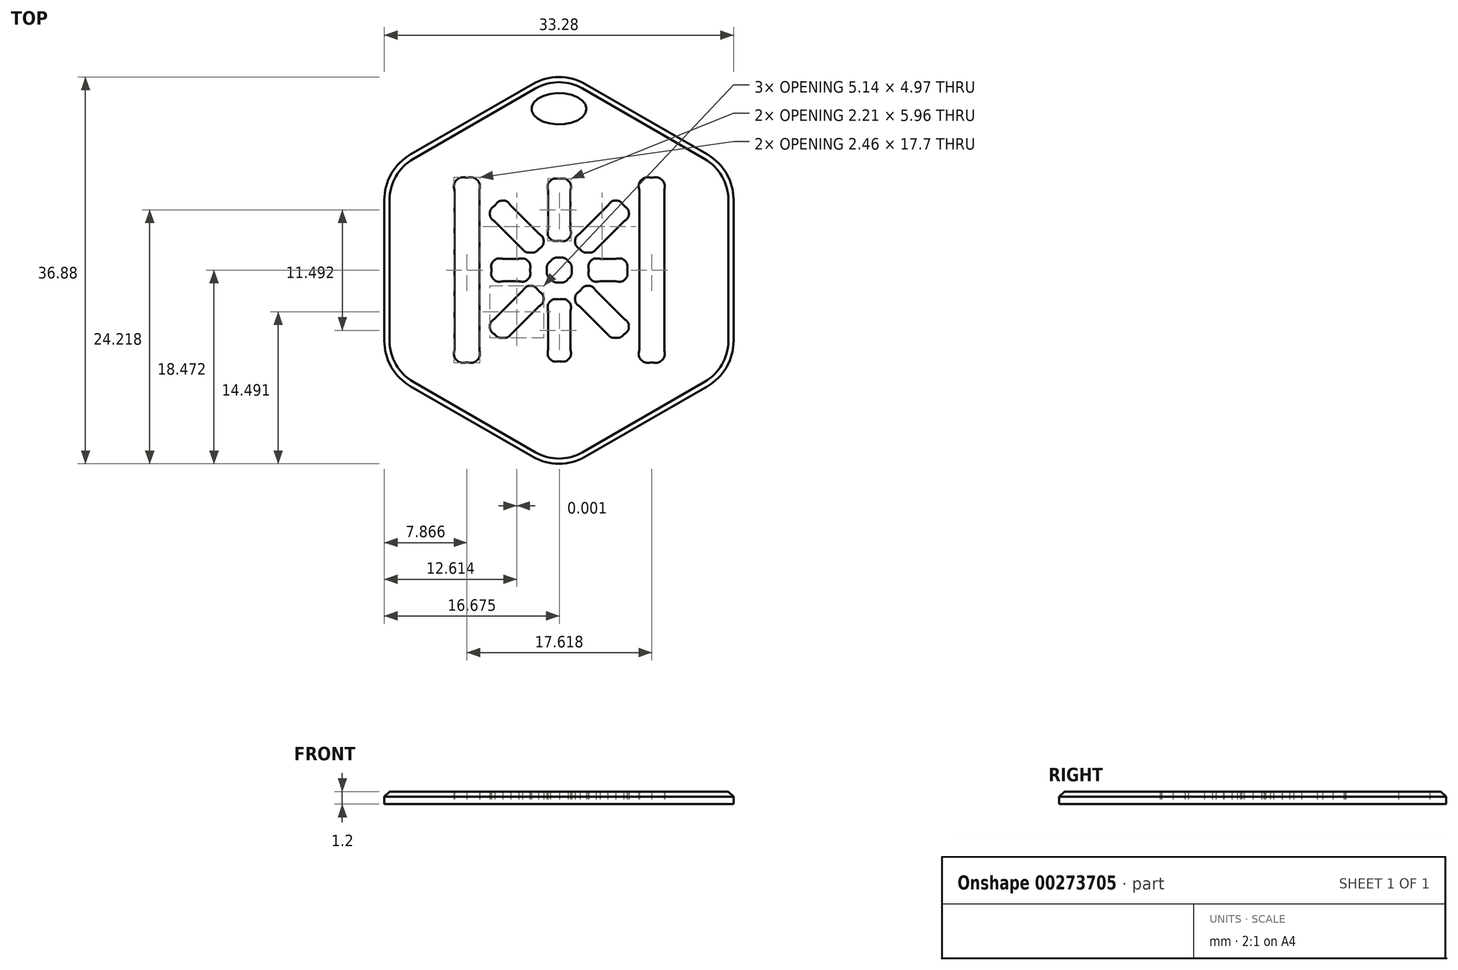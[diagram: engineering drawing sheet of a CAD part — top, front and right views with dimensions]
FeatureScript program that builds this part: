
annotation { "Feature Type Name" : "Feature", "Feature Type Description" : "" }
export const myFeature = defineFeature(function(context is Context, id is Id, definition is map)
    precondition{}
    {
        {
            var Q0;
            Q0=qCreatedBy(makeId("Top.planeOp"),FACE);
            var sketch = newSketch(context, id + "F0", { "sketchPlane" : qUnion([Q0])});
            skCircle(sketch, "E0.cCircle", {"center": v(0, 0) * mm, "radius": 16.64 * mm, "construction": true});
            skLineSegment(sketch, "E0.0", {"start": v(16.64, 6.72) * mm, "end": v(16.64, -6.72) * mm});
            skLineSegment(sketch, "E0.1", {"start": v(14.14, -11.05) * mm, "end": v(2.5, -17.77) * mm});
            skLineSegment(sketch, "E0.2", {"start": v(-2.5, -17.77) * mm, "end": v(-14.14, -11.05) * mm});
            skLineSegment(sketch, "E0.3", {"start": v(-16.64, -6.72) * mm, "end": v(-16.64, 6.72) * mm});
            skLineSegment(sketch, "E0.4", {"start": v(-14.14, 11.05) * mm, "end": v(-2.5, 17.77) * mm});
            skLineSegment(sketch, "E0.5", {"start": v(2.5, 17.77) * mm, "end": v(14.14, 11.05) * mm});
            skPoint(sketch, "E0.0.midPoint", {"position": v(16.64, 0) * mm});
            skPoint(sketch, "E1.visualSharp", {"position": v(-16.64, 9.6) * mm});
            skArc(sketch, "E1.filletArc", {"start": v(-14.14, 11.05) * mm, "mid": v(-15.97, 9.22) * mm, "end": v(-16.64, 6.72) * mm});
            skPoint(sketch, "E2.visualSharp", {"position": v(0, 19.22) * mm});
            skArc(sketch, "E2.filletArc", {"start": v(2.5, 17.77) * mm, "mid": v(0, 18.44) * mm, "end": v(-2.5, 17.77) * mm});
            skPoint(sketch, "E3.visualSharp", {"position": v(16.64, 9.6) * mm});
            skArc(sketch, "E3.filletArc", {"start": v(16.64, 6.72) * mm, "mid": v(15.97, 9.22) * mm, "end": v(14.14, 11.05) * mm});
            skPoint(sketch, "E4.visualSharp", {"position": v(16.64, -9.6) * mm});
            skArc(sketch, "E4.filletArc", {"start": v(14.14, -11.05) * mm, "mid": v(15.97, -9.22) * mm, "end": v(16.64, -6.72) * mm});
            skPoint(sketch, "E5.visualSharp", {"position": v(0, -19.22) * mm});
            skArc(sketch, "E5.filletArc", {"start": v(-2.5, -17.77) * mm, "mid": v(0, -18.44) * mm, "end": v(2.5, -17.77) * mm});
            skPoint(sketch, "E6.visualSharp", {"position": v(-16.64, -9.6) * mm});
            skArc(sketch, "E6.filletArc", {"start": v(-16.64, -6.72) * mm, "mid": v(-15.97, -9.22) * mm, "end": v(-14.14, -11.05) * mm});
            skPoint(sketch, "E7.visualSharp", {"position": v(-14.64, 8.45) * mm});
            skPoint(sketch, "E8.visualSharp", {"position": v(0, 16.9) * mm});
            skPoint(sketch, "E9.visualSharp", {"position": v(14.64, 8.45) * mm});
            skPoint(sketch, "E10.visualSharp", {"position": v(14.64, -8.45) * mm});
            skPoint(sketch, "E11.visualSharp", {"position": v(0, -16.9) * mm});
            skPoint(sketch, "E12.visualSharp", {"position": v(-14.64, -8.45) * mm});
            skFitSpline(sketch, "E13", {"points": [v(-5.35, -6.43) * mm, v(-5.63, -6.43) * mm, v(-5.9, -6.32) * mm, v(-6.1, -6.11) * mm]});
            skFitSpline(sketch, "E14", {"points": [v(-6.1, -6.11) * mm, v(-6.53, -5.7) * mm, v(-6.53, -5.02) * mm, v(-6.1, -4.6) * mm]});
            skFitSpline(sketch, "E15", {"points": [v(-3.47, -1.95) * mm, v(-3.05, -1.53) * mm, v(-2.37, -1.53) * mm, v(-1.94, -1.95) * mm]});
            skFitSpline(sketch, "E16", {"points": [v(-1.94, -1.95) * mm, v(-1.53, -2.37) * mm, v(-1.53, -3.05) * mm, v(-1.94, -3.47) * mm]});
            skLineSegment(sketch, "E17", {"start": v(-6.1, -4.6) * mm, "end": v(-3.47, -1.95) * mm});
            skFitSpline(sketch, "E18", {"points": [v(-4.6, -6.11) * mm, v(-4.8, -6.32) * mm, v(-5.07, -6.43) * mm, v(-5.35, -6.43) * mm]});
            skLineSegment(sketch, "E19", {"start": v(-1.94, -3.47) * mm, "end": v(-4.6, -6.11) * mm});
            skFitSpline(sketch, "E20", {"points": [v(3.91, -1.04) * mm, v(3.32, -1.04) * mm, v(2.84, -0.56) * mm, v(2.84, 0.03) * mm]});
            skFitSpline(sketch, "E21", {"points": [v(2.84, 0.03) * mm, v(2.84, 0.63) * mm, v(3.32, 1.1) * mm, v(3.91, 1.1) * mm]});
            skLineSegment(sketch, "E22", {"start": v(5.42, -1.04) * mm, "end": v(3.91, -1.04) * mm});
            skFitSpline(sketch, "E23", {"points": [v(5.42, 1.1) * mm, v(6.01, 1.1) * mm, v(6.5, 0.63) * mm, v(6.5, 0.03) * mm]});
            skFitSpline(sketch, "E24", {"points": [v(6.5, 0.03) * mm, v(6.5, -0.56) * mm, v(6.01, -1.04) * mm, v(5.42, -1.04) * mm]});
            skLineSegment(sketch, "E25", {"start": v(3.91, 1.1) * mm, "end": v(5.42, 1.1) * mm});
            skFitSpline(sketch, "E26", {"points": [v(-5.34, -1.04) * mm, v(-5.94, -1.04) * mm, v(-6.42, -0.56) * mm, v(-6.42, 0.03) * mm]});
            skFitSpline(sketch, "E27", {"points": [v(-6.42, 0.03) * mm, v(-6.42, 0.63) * mm, v(-5.94, 1.1) * mm, v(-5.34, 1.1) * mm]});
            skLineSegment(sketch, "E28", {"start": v(-3.84, -1.04) * mm, "end": v(-5.34, -1.04) * mm});
            skFitSpline(sketch, "E29", {"points": [v(-3.84, 1.1) * mm, v(-3.25, 1.1) * mm, v(-2.77, 0.63) * mm, v(-2.77, 0.03) * mm]});
            skFitSpline(sketch, "E30", {"points": [v(-2.77, 0.03) * mm, v(-2.77, -0.56) * mm, v(-3.25, -1.04) * mm, v(-3.84, -1.04) * mm]});
            skFitSpline(sketch, "E31", {"points": [v(5.42, -6.43) * mm, v(5.14, -6.43) * mm, v(4.87, -6.32) * mm, v(4.66, -6.11) * mm]});
            skLineSegment(sketch, "E32", {"start": v(-5.34, 1.1) * mm, "end": v(-3.84, 1.1) * mm});
            skFitSpline(sketch, "E33", {"points": [v(2.02, -3.47) * mm, v(1.6, -3.05) * mm, v(1.6, -2.37) * mm, v(2.02, -1.95) * mm]});
            skFitSpline(sketch, "E34", {"points": [v(2.02, -1.95) * mm, v(2.44, -1.53) * mm, v(3.12, -1.53) * mm, v(3.54, -1.95) * mm]});
            skLineSegment(sketch, "E35", {"start": v(4.66, -6.11) * mm, "end": v(2.02, -3.47) * mm});
            skFitSpline(sketch, "E36", {"points": [v(6.18, -4.6) * mm, v(6.6, -5.01) * mm, v(6.6, -5.7) * mm, v(6.18, -6.11) * mm]});
            skFitSpline(sketch, "E37", {"points": [v(6.18, -6.11) * mm, v(5.97, -6.32) * mm, v(5.7, -6.43) * mm, v(5.42, -6.43) * mm]});
            skFitSpline(sketch, "E38", {"points": [v(0.04, -8.66) * mm, v(-0.56, -8.66) * mm, v(-1.04, -8.18) * mm, v(-1.04, -7.59) * mm]});
            skLineSegment(sketch, "E39", {"start": v(3.54, -1.95) * mm, "end": v(6.18, -4.6) * mm});
            skFitSpline(sketch, "E40", {"points": [v(-1.04, -3.85) * mm, v(-1.04, -3.25) * mm, v(-0.56, -2.77) * mm, v(0.04, -2.77) * mm]});
            skFitSpline(sketch, "E41", {"points": [v(0.04, -2.77) * mm, v(0.63, -2.77) * mm, v(1.1, -3.25) * mm, v(1.1, -3.85) * mm]});
            skLineSegment(sketch, "E42", {"start": v(-1.04, -7.59) * mm, "end": v(-1.04, -3.85) * mm});
            skFitSpline(sketch, "E43", {"points": [v(1.1, -7.59) * mm, v(1.1, -8.18) * mm, v(0.63, -8.66) * mm, v(0.04, -8.66) * mm]});
            skFitSpline(sketch, "E44", {"points": [v(0.04, 2.83) * mm, v(-0.56, 2.83) * mm, v(-1.04, 3.32) * mm, v(-1.04, 3.9) * mm]});
            skLineSegment(sketch, "E45", {"start": v(1.1, -3.85) * mm, "end": v(1.1, -7.59) * mm});
            skFitSpline(sketch, "E46", {"points": [v(-1.04, 7.65) * mm, v(-1.04, 8.24) * mm, v(-0.56, 8.72) * mm, v(0.04, 8.72) * mm]});
            skFitSpline(sketch, "E47", {"points": [v(0.04, 8.72) * mm, v(0.63, 8.72) * mm, v(1.1, 8.24) * mm, v(1.1, 7.65) * mm]});
            skLineSegment(sketch, "E48", {"start": v(-1.04, 3.9) * mm, "end": v(-1.04, 7.65) * mm});
            skFitSpline(sketch, "E49", {"points": [v(1.1, 3.9) * mm, v(1.1, 3.32) * mm, v(0.63, 2.83) * mm, v(0.04, 2.83) * mm]});
            skFitSpline(sketch, "E50", {"points": [v(8.84, -8.78) * mm, v(8.18, -8.78) * mm, v(7.65, -8.24) * mm, v(7.65, -7.59) * mm]});
            skLineSegment(sketch, "E51", {"start": v(1.1, 7.65) * mm, "end": v(1.1, 3.9) * mm});
            skFitSpline(sketch, "E52", {"points": [v(7.65, 7.65) * mm, v(7.65, 8.3) * mm, v(8.18, 8.84) * mm, v(8.84, 8.84) * mm]});
            skFitSpline(sketch, "E53", {"points": [v(8.84, 8.84) * mm, v(9.5, 8.84) * mm, v(10.04, 8.3) * mm, v(10.04, 7.65) * mm]});
            skLineSegment(sketch, "E54", {"start": v(7.65, -7.59) * mm, "end": v(7.65, 7.65) * mm});
            skFitSpline(sketch, "E55", {"points": [v(10.04, -7.59) * mm, v(10.04, -8.24) * mm, v(9.5, -8.78) * mm, v(8.84, -8.78) * mm]});
            skFitSpline(sketch, "E56", {"points": [v(2.78, 1.7) * mm, v(2.5, 1.7) * mm, v(2.23, 1.8) * mm, v(2.02, 2.01) * mm]});
            skFitSpline(sketch, "E57", {"points": [v(2.02, 2.01) * mm, v(1.6, 2.43) * mm, v(1.6, 3.11) * mm, v(2.02, 3.53) * mm]});
            skLineSegment(sketch, "E58", {"start": v(10.04, 7.65) * mm, "end": v(10.04, -7.59) * mm});
            skFitSpline(sketch, "E59", {"points": [v(4.66, 6.18) * mm, v(5.08, 6.6) * mm, v(5.76, 6.6) * mm, v(6.18, 6.18) * mm]});
            skFitSpline(sketch, "E60", {"points": [v(6.18, 6.18) * mm, v(6.6, 5.76) * mm, v(6.6, 5.08) * mm, v(6.18, 4.66) * mm]});
            skLineSegment(sketch, "E61", {"start": v(2.02, 3.53) * mm, "end": v(4.66, 6.18) * mm});
            skFitSpline(sketch, "E62", {"points": [v(3.54, 2.02) * mm, v(3.33, 1.8) * mm, v(3.05, 1.7) * mm, v(2.78, 1.7) * mm]});
            skFitSpline(sketch, "E63", {"points": [v(-2.7, 1.7) * mm, v(-2.98, 1.7) * mm, v(-3.25, 1.8) * mm, v(-3.47, 2.01) * mm]});
            skLineSegment(sketch, "E64", {"start": v(6.18, 4.66) * mm, "end": v(3.54, 2.02) * mm});
            skFitSpline(sketch, "E65", {"points": [v(-6.1, 4.66) * mm, v(-6.53, 5.08) * mm, v(-6.53, 5.76) * mm, v(-6.1, 6.18) * mm]});
            skFitSpline(sketch, "E66", {"points": [v(-6.1, 6.18) * mm, v(-5.69, 6.6) * mm, v(-5, 6.6) * mm, v(-4.6, 6.18) * mm]});
            skLineSegment(sketch, "E67", {"start": v(-3.47, 2.01) * mm, "end": v(-6.1, 4.66) * mm});
            skFitSpline(sketch, "E68", {"points": [v(-1.95, 3.53) * mm, v(-1.53, 3.11) * mm, v(-1.53, 2.43) * mm, v(-1.95, 2.01) * mm]});
            skFitSpline(sketch, "E69", {"points": [v(-1.95, 2.01) * mm, v(-2.15, 1.8) * mm, v(-2.43, 1.7) * mm, v(-2.7, 1.7) * mm]});
            skFitSpline(sketch, "E70", {"points": [v(0.04, -1.16) * mm, v(-0.28, -1.16) * mm, v(-0.59, -1.03) * mm, v(-0.8, -0.81) * mm]});
            skFitSpline(sketch, "E71", {"points": [v(-0.8, -0.81) * mm, v(-1.03, -0.59) * mm, v(-1.16, -0.28) * mm, v(-1.16, 0.03) * mm]});
            skFitSpline(sketch, "E72", {"points": [v(-1.16, 0.03) * mm, v(-1.16, 0.35) * mm, v(-1.03, 0.65) * mm, v(-0.8, 0.87) * mm]});
            skFitSpline(sketch, "E73", {"points": [v(-0.8, 0.87) * mm, v(-0.59, 1.1) * mm, v(-0.28, 1.22) * mm, v(0.04, 1.22) * mm]});
            skFitSpline(sketch, "E74", {"points": [v(0.04, 1.22) * mm, v(0.35, 1.22) * mm, v(0.66, 1.1) * mm, v(0.88, 0.87) * mm]});
            skFitSpline(sketch, "E75", {"points": [v(0.88, 0.87) * mm, v(1.1, 0.65) * mm, v(1.23, 0.35) * mm, v(1.23, 0.03) * mm]});
            skFitSpline(sketch, "E76", {"points": [v(1.23, 0.03) * mm, v(1.23, -0.28) * mm, v(1.1, -0.59) * mm, v(0.88, -0.81) * mm]});
            skFitSpline(sketch, "E77", {"points": [v(0.88, -0.81) * mm, v(0.66, -1.03) * mm, v(0.35, -1.16) * mm, v(0.04, -1.16) * mm]});
            skFitSpline(sketch, "E78", {"points": [v(-8.77, -8.78) * mm, v(-9.43, -8.78) * mm, v(-9.96, -8.24) * mm, v(-9.96, -7.59) * mm]});
            skLineSegment(sketch, "E79", {"start": v(-4.6, 6.18) * mm, "end": v(-1.95, 3.53) * mm});
            skFitSpline(sketch, "E80", {"points": [v(-9.96, 7.65) * mm, v(-9.96, 8.3) * mm, v(-9.43, 8.84) * mm, v(-8.77, 8.84) * mm]});
            skFitSpline(sketch, "E81", {"points": [v(-8.77, 8.84) * mm, v(-8.11, 8.84) * mm, v(-7.58, 8.3) * mm, v(-7.58, 7.65) * mm]});
            skLineSegment(sketch, "E82", {"start": v(-9.96, -7.59) * mm, "end": v(-9.96, 7.65) * mm});
            skFitSpline(sketch, "E83", {"points": [v(-7.58, -7.59) * mm, v(-7.58, -8.24) * mm, v(-8.11, -8.78) * mm, v(-8.77, -8.78) * mm]});
            skLineSegment(sketch, "E84", {"start": v(-7.58, 7.65) * mm, "end": v(-7.58, -7.59) * mm});
            skEllipse(sketch, "E85", {"center": v(0, 15.41) * mm, "majorRadius": 2.6 * mm, "minorRadius": 1.5 * mm, "majorAxis": v(1, 0)});
            skSolve(sketch);
        }
        {
            var Q0;
            Q0 = qSketchRegion(id + "F0", true);
            extrude(context, id + "F1", {"entities" : qUnion([Q0]), "depth" : 1.2 * mm});
        }
        {
            var Q0;
            Q0=makeQuery(id+"F1.opExtrude","CAP_EDGE",EDGE,{"disambiguationData":[OSD([sQuery(id+"F0.wireOp",EDGE,"E0.2")])],"isStart":false});
            chamfer(context, id + "F2", {"entities" : qUnion([Q0]), "width" : 0.5 * mm, "tangentPropagation" : true});
        }
    });
